# Revit family: 201_PR-LDS-_-_-_+LDS
name_source: partatom
category: Air Terminals
units: mm (PartAtom-declared; Revit-internal decimal feet)

## family parameters
Always vertical = Yes
Cut with Voids When Loaded = No
Part Type = Normal
Room Calculation Point = Yes
Round Connector Dimension = Use Diameter
Shared = No
Work Plane-Based = No

## types (5) — shared parameters
CAT0 = Yes
CL_Location_5000 = 5000 mm  [stored 16.4042 ft]
Description = PLENUM BOXES FOR PR-LDS
HT = 4 mm  [stored 0.0131234 ft]
L_ARR = 400 mm  [stored 1.31234 ft]
Manufacturer = Alnor
QmdConnectorList = 201;D
URL = http://www.ventilation-alnor.co.uk
W_ARR = 400 mm  [stored 1.31234 ft]
XRefLineVPlnId = 7453
YRefLineVPlnId = 7456
Z1 = 2 mm  [stored 0.00656168 ft]
Z1__ve = -2 mm  [stored -0.00656168 ft]
magiPartTypeId = 201
magiProductFamilyId = PR-LDS-*-*-*+LDS
zero-valued in all types: CLBTZ, H_ARR

## per-type parameters (varying)
| type | A12 | BB2 | BN2 | D | HN2 | W2 | YD | ZT | ZTD | magiProductId |
| PR-LDS 1-495 125 | 40 mm  [stored 0.131234 ft] | 245 mm  [stored 0.803806 ft] | 248 mm | 125 mm | 22 mm  [stored 0.0721785 ft] | 23 mm | 266 mm | 200 mm  [stored 0.656168 ft] | 87 mm | PR-LDS-1-495-125+LDS |
| PR-LDS 4-990 200 | 106 mm | 493 mm | 495 mm  [stored 1.62402 ft] | 200 mm | 88 mm | 93 mm | 513 mm | 250 mm | 124 mm | PR-LDS-4-990-200+LDS |
| PR-LDS 3-990 200 | 84 mm | 493 mm | 495 mm  [stored 1.62402 ft] | 200 mm | 66 mm | 70 mm | 513 mm | 250 mm | 124 mm | PR-LDS-3-990-200+LDS |
| PR-LDS 2-990 160 | 62 mm | 493 mm | 495 mm  [stored 1.62402 ft] | 160 mm | 44 mm  [stored 0.144357 ft] | 45 mm  [stored 0.147638 ft] | 513 mm | 200 mm  [stored 0.656168 ft] | 104 mm | PR-LDS-2-990-160+LDS |
| PR-LDS 2-495 160 | 62 mm | 245 mm  [stored 0.803806 ft] | 248 mm | 160 mm | 44 mm  [stored 0.144357 ft] | 45 mm  [stored 0.147638 ft] | 266 mm | 200 mm  [stored 0.656168 ft] | 104 mm | PR-LDS-2-495-160+LDS |

note: column(s) folded — value = type name in every type: MC Product Code

note: [stored X ft] marks values corroborated as IEEE doubles in the binary element streams (Revit-internal decimal feet)

## geometry (parser evidence)
native form markers: Blend x2, Sweep x2
no freeform markers — native parametric forms only
